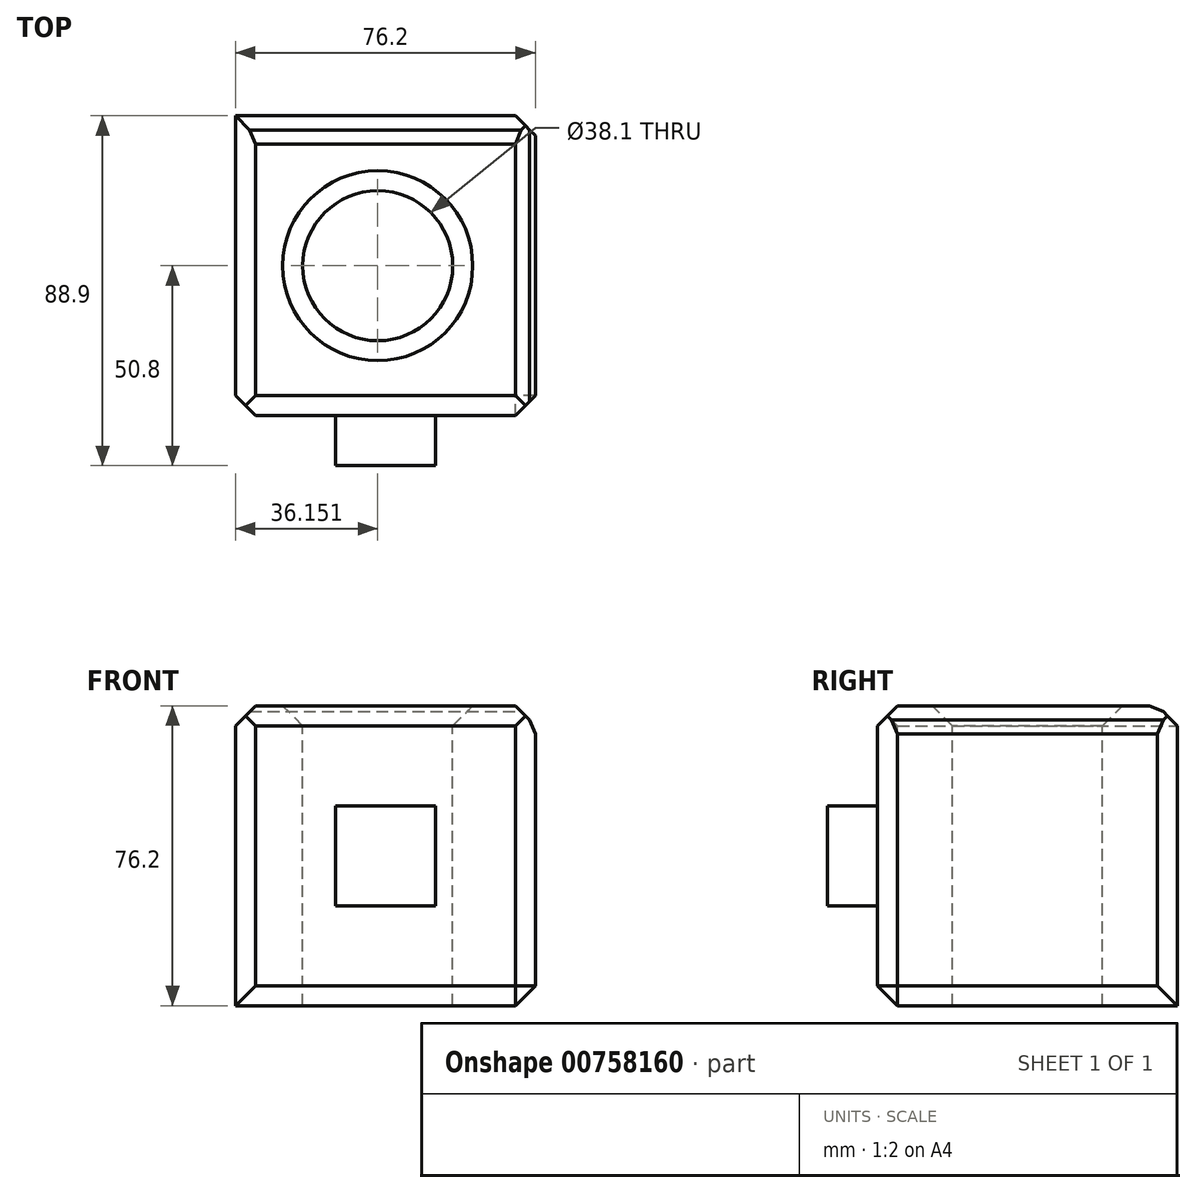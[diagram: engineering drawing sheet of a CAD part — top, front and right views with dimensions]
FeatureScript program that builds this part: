
annotation { "Feature Type Name" : "Feature", "Feature Type Description" : "" }
export const myFeature = defineFeature(function(context is Context, id is Id, definition is map)
    precondition{}
    {
        {
            var Q0;
            Q0=qCreatedBy(makeId("Front.planeOp"),FACE);
            var sketch = newSketch(context, id + "F0", { "sketchPlane" : qUnion([Q0])});
            skLineSegment(sketch, "E0.bottom", {"start": v(0, 0) * mm, "end": v(76.2, 0) * mm});
            skLineSegment(sketch, "E0.top", {"start": v(0, 76.2) * mm, "end": v(76.2, 76.2) * mm});
            skLineSegment(sketch, "E0.left", {"start": v(0, 0) * mm, "end": v(0, 76.2) * mm});
            skLineSegment(sketch, "E0.right", {"start": v(76.2, 0) * mm, "end": v(76.2, 76.2) * mm});
            skSolve(sketch);
        }
        {
            var Q0;
            Q0=makeQuery(id+"F0.imprint","IMPRINT",FACE,{"disambiguationData":[TD([[makeQuery(id+"F0.imprint","IMPRINT",EDGE,{"derivedFrom":sQuery(id+"F0.wireOp",EDGE,"E0.bottom")}),1.0]])]});
            extrude(context, id + "F1", {"entities" : qUnion([Q0]), "depth" : 76.2 * mm, "offsetDistance" : 25.4 * mm});
        }
        {
            var Q0;
            Q0=makeQuery(id+"F1.opExtrude","SWEPT_FACE",FACE,{"disambiguationData":[OSD([sQuery(id+"F0.wireOp",EDGE,"E0.top")])]});
            var sketch = newSketch(context, id + "F2", { "sketchPlane" : qUnion([Q0])});
            skPoint(sketch, "E1", {"position": v(36.15, -38.1) * mm});
            skSolve(sketch);
        }
        {
            var Q0;
            Q0=sQuery(id+"F2.wireOp",VERTEX,"E1");
            var Q1;
            Q1=makeQuery(id+"F1.opExtrude","SWEPT_BODY",BODY,{"disambiguationData":[OSD([sQuery(id+"F0.wireOp",EDGE,"E0.bottom"),sQuery(id+"F0.wireOp",EDGE,"E0.top"),sQuery(id+"F0.wireOp",EDGE,"E0.left"),sQuery(id+"F0.wireOp",EDGE,"E0.right")])]});
            hole(context, id + "F3", {"style" : HoleStyle.SIMPLE, "endStyle" : HoleEndStyle.THROUGH, "holeDiameter" : 38.1 * mm, "majorDiameter" : 6.35 * mm, "isTappedThrough" : true, "tappedDepth" : 12.7 * mm, "tapClearance" : 3, "locations" : qUnion([Q0]), "scope" : qUnion([Q1])});
        }
        {
            var Q0;
            Q0=makeQuery(id+"F1.opExtrude","CAP_FACE",FACE,{"disambiguationData":[OSD([sQuery(id+"F0.wireOp",EDGE,"E0.bottom"),sQuery(id+"F0.wireOp",EDGE,"E0.top"),sQuery(id+"F0.wireOp",EDGE,"E0.left"),sQuery(id+"F0.wireOp",EDGE,"E0.right")])],"isStart":false});
            var sketch = newSketch(context, id + "F4", { "sketchPlane" : qUnion([Q0])});
            skPoint(sketch, "E2", {"position": v(38.1, 38.1) * mm});
            skSolve(sketch);
        }
        {
            var Q0;
            Q0=makeQuery(id+"F4.imprint","IMPRINT",FACE,{"disambiguationData":[TD([[makeQuery(id+"F4.imprint","IMPRINT",EDGE,{"derivedFrom":makeQuery(id+"F1.opExtrude","CAP_EDGE",EDGE,{"disambiguationData":[OSD([sQuery(id+"F0.wireOp",EDGE,"E0.bottom")])],"isStart":false})}),1.0]])]});
            var sketch = newSketch(context, id + "F5", { "sketchPlane" : qUnion([Q0])});
            skLineSegment(sketch, "E3.bottom", {"start": v(25.4, 25.4) * mm, "end": v(50.8, 25.4) * mm});
            skLineSegment(sketch, "E3.top", {"start": v(25.4, 50.8) * mm, "end": v(50.8, 50.8) * mm});
            skLineSegment(sketch, "E3.left", {"start": v(25.4, 25.4) * mm, "end": v(25.4, 50.8) * mm});
            skLineSegment(sketch, "E3.right", {"start": v(50.8, 25.4) * mm, "end": v(50.8, 50.8) * mm});
            skPoint(sketch, "E3.middle", {"position": v(38.1, 38.1) * mm});
            skSolve(sketch);
        }
        {
            var Q0;
            Q0 = qSketchRegion(id + "F5", true);
            extrude(context, id + "F6", {"entities" : qUnion([Q0]), "operationType" : NewBodyOperationType.ADD, "depth" : 12.7 * mm, "offsetDistance" : 25.4 * mm});
        }
        {
            var Q0;
            Q0=makeQuery(id+"F1.opExtrude","SWEPT_EDGE",EDGE,{"disambiguationData":[OSD([sQuery(id+"F0.wireOp",EDGE,"E0.top"),sQuery(id+"F0.wireOp",EDGE,"E0.left")])]});
            var Q1;
            Q1=makeQuery(id+"F1.opExtrude","SWEPT_EDGE",EDGE,{"disambiguationData":[OSD([sQuery(id+"F0.wireOp",EDGE,"E0.top"),sQuery(id+"F0.wireOp",EDGE,"E0.right")])]});
            var Q2;
            Q2=makeQuery(id+"F1.opExtrude","SWEPT_FACE",FACE,{"disambiguationData":[OSD([sQuery(id+"F0.wireOp",EDGE,"E0.top")])]});
            chamfer(context, id + "F7", {"entities" : qUnion([Q0, Q1, Q2]), "width" : 5.08 * mm, "tangentPropagation" : true});
        }
        {
            var Q0;
            Q0=makeQuery(id+"F1.opExtrude","CAP_EDGE",EDGE,{"disambiguationData":[OSD([sQuery(id+"F0.wireOp",EDGE,"E0.left")])],"isStart":false});
            var Q1;
            Q1=makeQuery(id+"F1.opExtrude","CAP_EDGE",EDGE,{"disambiguationData":[OSD([sQuery(id+"F0.wireOp",EDGE,"E0.right")])],"isStart":false});
            var Q2;
            {var subQ0=sQuery(id+"F0.wireOp",EDGE,"E0.right");Q2=makeQuery(id+"F7.opChamfer","BLEND_EDGE",EDGE,{"blendedFrom":[makeQuery(id+"F1.opExtrude","SWEPT_EDGE",EDGE,{"disambiguationData":[OSD([sQuery(id+"F0.wireOp",EDGE,"E0.top"),subQ0])]}),makeQuery(id+"F1.opExtrude","SWEPT_FACE",FACE,{"disambiguationData":[OSD([subQ0])]})],"blendedInto":[makeQuery(id+"F1.opExtrude","SWEPT_FACE",FACE,{"disambiguationData":[OSD([subQ0])]})]});}
            var Q3;
            Q3=makeQuery(id+"F1.opExtrude","SWEPT_EDGE",EDGE,{"disambiguationData":[OSD([sQuery(id+"F0.wireOp",EDGE,"E0.bottom"),sQuery(id+"F0.wireOp",EDGE,"E0.right")])]});
            var Q4;
            Q4=makeQuery(id+"F1.opExtrude","SWEPT_FACE",FACE,{"disambiguationData":[OSD([sQuery(id+"F0.wireOp",EDGE,"E0.right")])]});
            var Q5;
            Q5=makeQuery(id+"F1.opExtrude","CAP_EDGE",EDGE,{"disambiguationData":[OSD([sQuery(id+"F0.wireOp",EDGE,"E0.bottom")])],"isStart":false});
            var Q6;
            {var subQ0=sQuery(id+"F0.wireOp",EDGE,"E0.top");Q6=makeQuery(id+"F7.opChamfer","BLEND_EDGE",EDGE,{"blendedFrom":[makeQuery(id+"F1.opExtrude","CAP_EDGE",EDGE,{"disambiguationData":[OSD([subQ0])],"isStart":true}),makeQuery(id+"F1.opExtrude","SWEPT_FACE",FACE,{"disambiguationData":[OSD([subQ0])]})],"blendedInto":[makeQuery(id+"F1.opExtrude","SWEPT_FACE",FACE,{"disambiguationData":[OSD([subQ0])]})]});}
            chamfer(context, id + "F8", {"entities" : qUnion([Q0, Q1, Q2, Q3, Q4, Q5, Q6]), "width" : 5.08 * mm, "tangentPropagation" : true});
        }
    });
